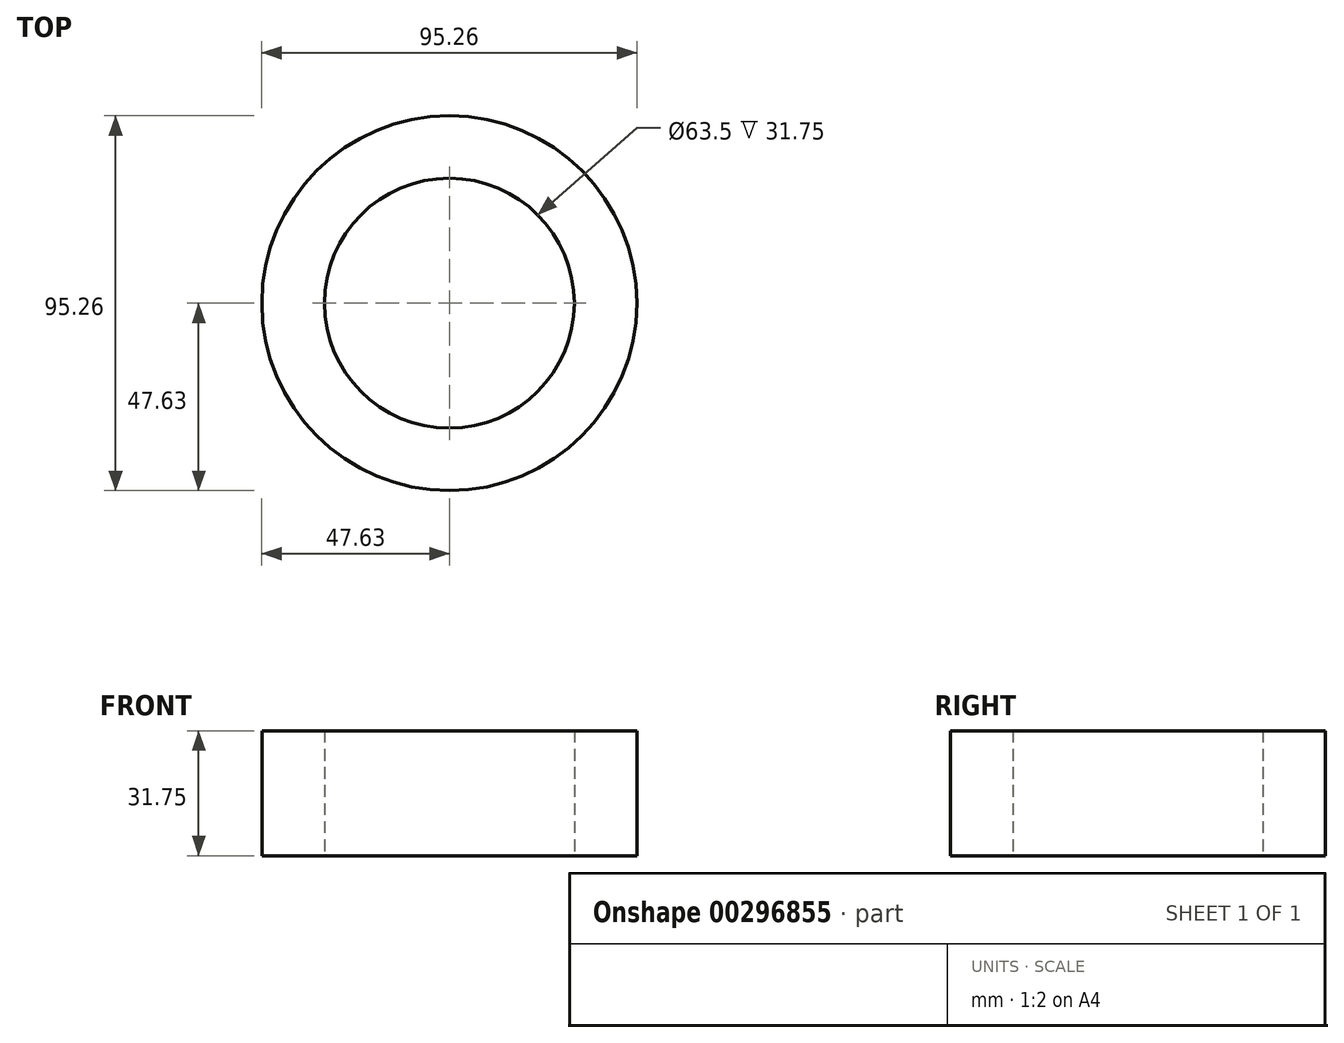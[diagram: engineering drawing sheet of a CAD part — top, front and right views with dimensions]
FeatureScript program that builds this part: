
annotation { "Feature Type Name" : "Feature", "Feature Type Description" : "" }
export const myFeature = defineFeature(function(context is Context, id is Id, definition is map)
    precondition{}
    {
        {
            var Q0;
            Q0=qCreatedBy(makeId("Top.planeOp"),FACE);
            var sketch = newSketch(context, id + "F0", { "sketchPlane" : qUnion([Q0])});
            skCircle(sketch, "E0", {"center": v(0, 0) * mm, "radius": 47.63 * mm});
            skCircle(sketch, "E1", {"center": v(0, 0) * mm, "radius": 31.75 * mm});
            skLineSegment(sketch, "E2", {"start": v(-33.68, 33.68) * mm, "end": v(-22.45, 22.45) * mm});
            skLineSegment(sketch, "E3.trimOffspring", {"start": v(22.45, -22.45) * mm, "end": v(33.68, -33.68) * mm});
            skSolve(sketch);
        }
        {
            var Q0;
            {var subQ0=sQuery(id+"F0.wireOp",EDGE,"E2");Q0=makeQuery(id+"F0.imprint","IMPRINT",FACE,{"disambiguationData":[TD([[makeQuery(id+"F0.imprint","IMPRINT",EDGE,{"derivedFrom":subQ0}),1.0]])]});}
            extrude(context, id + "F1", {"entities" : qUnion([Q0]), "depth" : 25.4 * mm});
        }
        {
            var Q0;
            {var subQ0=sQuery(id+"F0.wireOp",EDGE,"E2");Q0=makeQuery(id+"F0.imprint","IMPRINT",FACE,{"disambiguationData":[TD([[makeQuery(id+"F0.imprint","IMPRINT",EDGE,{"derivedFrom":subQ0}),-1.0]])]});}
            extrude(context, id + "F2", {"entities" : qUnion([Q0]), "depth" : 31.75 * mm});
        }
        {
            var Q0;
            Q0=makeQuery(id+"F1.opExtrude","CAP_FACE",FACE,{"disambiguationData":[OSD([sQuery(id+"F0.wireOp",EDGE,"E0"),sQuery(id+"F0.wireOp",EDGE,"E1"),sQuery(id+"F0.wireOp",EDGE,"E2"),sQuery(id+"F0.wireOp",EDGE,"E3.trimOffspring")])],"isStart":false});
            extrude(context, id + "F3", {"entities" : qUnion([Q0]), "operationType" : NewBodyOperationType.ADD, "depth" : 6.35 * mm});
        }
    });
